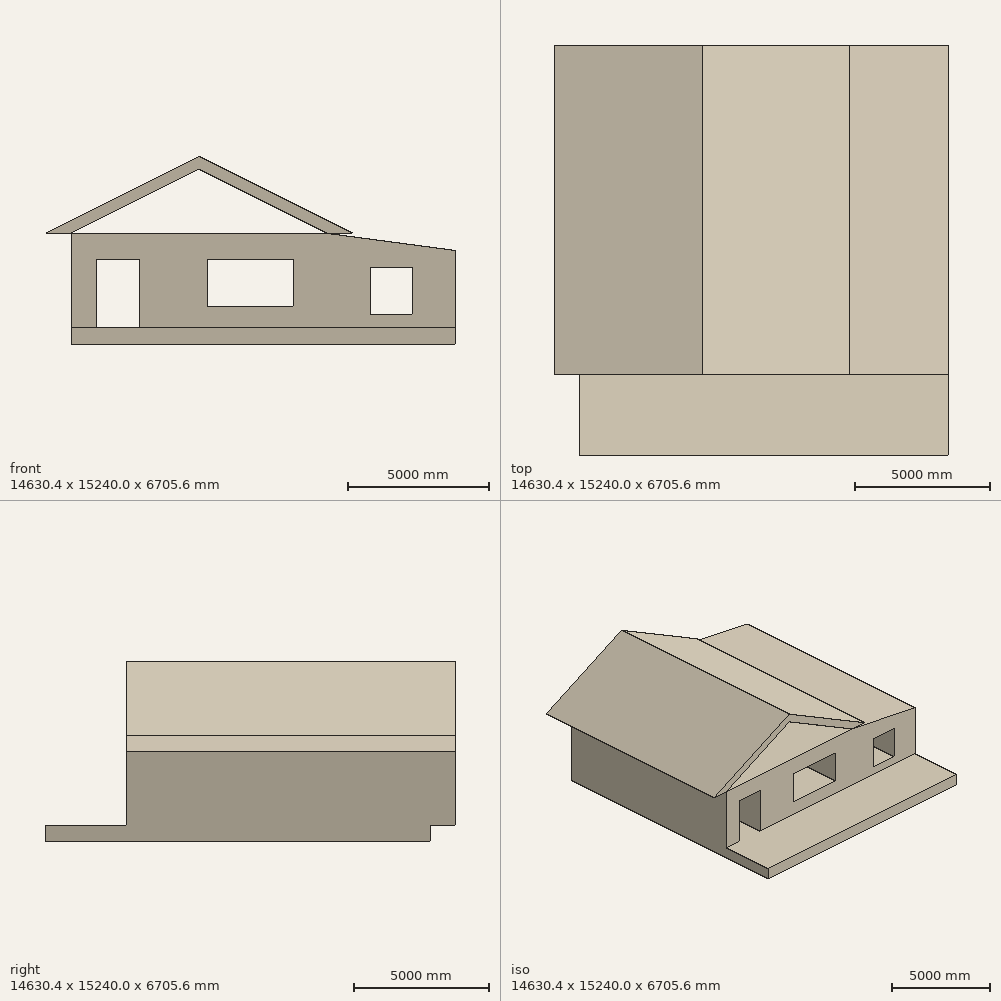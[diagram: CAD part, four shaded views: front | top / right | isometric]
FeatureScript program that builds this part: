
annotation { "Feature Type Name" : "Feature", "Feature Type Description" : "" }
export const myFeature = defineFeature(function(context is Context, id is Id, definition is map)
    precondition{}
    {
        {
            var Q0;
            Q0=qCreatedBy(makeId("Front.planeOp"),FACE);
            var sketch = newSketch(context, id + "F0", { "sketchPlane" : qUnion([Q0])});
            skLineSegment(sketch, "E0", {"start": v(0, 0) * mm, "end": v(-4572, 0) * mm});
            skLineSegment(sketch, "E1", {"start": v(0, 0) * mm, "end": v(4572, 0) * mm});
            skLineSegment(sketch, "E2", {"start": v(0, 0) * mm, "end": v(0, 2286) * mm, "construction": true});
            skLineSegment(sketch, "E3", {"start": v(-4572, 0) * mm, "end": v(-5486.4, 0) * mm});
            skLineSegment(sketch, "E4", {"start": v(4572, 0) * mm, "end": v(5486.4, 0) * mm});
            skLineSegment(sketch, "E5", {"start": v(-4572, 0) * mm, "end": v(0, 2286) * mm});
            skLineSegment(sketch, "E6", {"start": v(4572, 0) * mm, "end": v(0, 2286) * mm});
            skLineSegment(sketch, "E7", {"start": v(0, 2286) * mm, "end": v(0, 2743.2) * mm});
            skLineSegment(sketch, "E8", {"start": v(-5486.4, 0) * mm, "end": v(0, 2743.2) * mm});
            skLineSegment(sketch, "E9", {"start": v(5486.4, 0) * mm, "end": v(0, 2743.2) * mm});
            skLineSegment(sketch, "E10", {"start": v(-4572, 0) * mm, "end": v(-4572, -3352.8) * mm});
            skLineSegment(sketch, "E11", {"start": v(-4572, -3352.8) * mm, "end": v(4572, -3352.8) * mm});
            skLineSegment(sketch, "E12", {"start": v(4572, 0) * mm, "end": v(4572, -3352.8) * mm});
            skLineSegment(sketch, "E13", {"start": v(-4572, -3352.8) * mm, "end": v(-4572, -3962.4) * mm});
            skLineSegment(sketch, "E14", {"start": v(-4572, -3962.4) * mm, "end": v(4572, -3962.4) * mm});
            skLineSegment(sketch, "E15", {"start": v(4572, -3352.8) * mm, "end": v(4572, -3962.4) * mm});
            skLineSegment(sketch, "E16", {"start": v(4572, -3352.8) * mm, "end": v(9144, -3352.8) * mm});
            skLineSegment(sketch, "E17", {"start": v(4572, -3962.4) * mm, "end": v(9144, -3962.4) * mm});
            skLineSegment(sketch, "E18", {"start": v(9144, -3352.8) * mm, "end": v(9144, -3962.4) * mm});
            skLineSegment(sketch, "E19", {"start": v(9144, -3352.8) * mm, "end": v(9144, -609.6) * mm});
            skLineSegment(sketch, "E20", {"start": v(9144, -609.6) * mm, "end": v(4572, 0) * mm});
            skLineSegment(sketch, "E21", {"start": v(9144, -609.6) * mm, "end": v(9144, -1219.2) * mm});
            skLineSegment(sketch, "E22", {"start": v(9144, -1219.2) * mm, "end": v(4572.83, -609.71) * mm});
            skLineSegment(sketch, "E23", {"start": v(-3352.8, -3352.8) * mm, "end": v(-3352.8, -1219.2) * mm});
            skLineSegment(sketch, "E24", {"start": v(-3352.8, -1219.2) * mm, "end": v(-2438.4, -1219.2) * mm});
            skLineSegment(sketch, "E25", {"start": v(-2438.4, -1219.2) * mm, "end": v(-2438.4, -3352.8) * mm});
            skLineSegment(sketch, "E26.0", {"start": v(-2133.6, -914.4) * mm, "end": v(-2133.6, -3352.8) * mm});
            skLineSegment(sketch, "E26.1", {"start": v(-3657.6, -914.4) * mm, "end": v(-2133.6, -914.4) * mm});
            skLineSegment(sketch, "E26.2", {"start": v(-3657.6, -3353.8) * mm, "end": v(-3657.6, -914.4) * mm});
            skLineSegment(sketch, "E27.bottom", {"start": v(457.2, -1066.8) * mm, "end": v(3200.4, -1066.8) * mm});
            skLineSegment(sketch, "E27.top", {"start": v(457.2, -2438.4) * mm, "end": v(3200.4, -2438.4) * mm});
            skLineSegment(sketch, "E27.left", {"start": v(457.2, -1066.8) * mm, "end": v(457.2, -2438.4) * mm});
            skLineSegment(sketch, "E27.right", {"start": v(3200.4, -1066.8) * mm, "end": v(3200.4, -2438.4) * mm});
            skLineSegment(sketch, "E28.0", {"start": v(304.8, -2590.8) * mm, "end": v(3352.8, -2590.8) * mm});
            skLineSegment(sketch, "E28.1", {"start": v(304.8, -914.4) * mm, "end": v(304.8, -2590.8) * mm});
            skLineSegment(sketch, "E28.2", {"start": v(304.8, -914.4) * mm, "end": v(3352.8, -914.4) * mm});
            skLineSegment(sketch, "E28.3", {"start": v(3352.8, -914.4) * mm, "end": v(3352.8, -2590.8) * mm});
            skLineSegment(sketch, "E29.bottom", {"start": v(6248.4, -1371.6) * mm, "end": v(7467.6, -1371.6) * mm});
            skLineSegment(sketch, "E29.top", {"start": v(6248.4, -2743.2) * mm, "end": v(7467.6, -2743.2) * mm});
            skLineSegment(sketch, "E29.left", {"start": v(6248.4, -1371.6) * mm, "end": v(6248.4, -2743.2) * mm});
            skLineSegment(sketch, "E29.right", {"start": v(7467.6, -1371.6) * mm, "end": v(7467.6, -2743.2) * mm});
            skLineSegment(sketch, "E30.0", {"start": v(6096, -2895.6) * mm, "end": v(7620, -2895.6) * mm});
            skLineSegment(sketch, "E30.1", {"start": v(6096, -1219.2) * mm, "end": v(6096, -2895.6) * mm});
            skLineSegment(sketch, "E30.2", {"start": v(6096, -1219.2) * mm, "end": v(7620, -1219.2) * mm});
            skLineSegment(sketch, "E30.3", {"start": v(7620, -1219.2) * mm, "end": v(7620, -2895.6) * mm});
            skText(sketch, "E31", { "text": "Property of Whitney Gates", "fontName": "OpenSans-Regular.ttf"});
            const initialGuessF0  = {"E31": [-6.10782, 3.01593, 1, 0, 1.31451]};
            skSetInitialGuess(sketch, initialGuessF0);
            skSolve(sketch);
        }
        {
            var Q0;
            Q0=makeQuery(id+"F0.imprint","IMPRINT",FACE,{"disambiguationData":[TD([[makeQuery(id+"F0.imprint","IMPRINT",EDGE,{"derivedFrom":sQuery(id+"F0.wireOp",EDGE,"E3")}),-1.0]])]});
            var Q1;
            Q1=makeQuery(id+"F0.imprint","IMPRINT",FACE,{"disambiguationData":[TD([[makeQuery(id+"F0.imprint","IMPRINT",EDGE,{"derivedFrom":sQuery(id+"F0.wireOp",EDGE,"E4")}),1.0]])]});
            extrude(context, id + "F1", {"entities" : qUnion([Q0, Q1]), "depth" : 30.48 * mm, "offsetDistance" : 30.48 * mm, "hasSecondDirection" : true, "secondDirectionOppositeDirection" : true, "secondDirectionDepth" : 12192 * mm});
        }
        {
            var Q0;
            Q0=makeQuery(id+"F0.imprint","IMPRINT",FACE,{"disambiguationData":[TD([[makeQuery(id+"F0.imprint","IMPRINT",EDGE,{"derivedFrom":sQuery(id+"F0.wireOp",EDGE,"E15")}),1.0]])]});
            var Q1;
            {var subQ5=sQuery(id+"F0.wireOp",EDGE,"E13");Q1=makeQuery(id+"F0.imprint","IMPRINT",FACE,{"disambiguationData":[TD([[makeQuery(id+"F0.imprint","IMPRINT",EDGE,{"derivedFrom":subQ5}),1.0]])]});}
            extrude(context, id + "F2", {"entities" : qUnion([Q0, Q1]), "depth" : 3048 * mm, "offsetDistance" : 30.48 * mm, "hasSecondDirection" : true, "secondDirectionOppositeDirection" : true, "secondDirectionDepth" : 11277.6 * mm});
        }
        {
            var Q0;
            Q0=makeQuery(id+"F0.imprint","IMPRINT",FACE,{"disambiguationData":[TD([[makeQuery(id+"F0.imprint","IMPRINT",EDGE,{"derivedFrom":sQuery(id+"F0.wireOp",EDGE,"E12")}),1.0]])]});
            extrude(context, id + "F3", {"entities" : qUnion([Q0]), "operationType" : NewBodyOperationType.ADD, "oppositeDirection" : true, "depth" : 12192 * mm, "offsetDistance" : 30.48 * mm, "hasSecondDirection" : true, "secondDirectionOppositeDirection" : false, "secondDirectionDepth" : 30.48 * mm});
        }
        {
            var Q0;
            Q0=makeQuery(id+"F0.imprint","IMPRINT",FACE,{"disambiguationData":[TD([[makeQuery(id+"F0.imprint","IMPRINT",EDGE,{"derivedFrom":sQuery(id+"F0.wireOp",EDGE,"E0")}),1.0]])]});
            extrude(context, id + "F4", {"entities" : qUnion([Q0]), "operationType" : NewBodyOperationType.ADD, "oppositeDirection" : true, "depth" : 11277.6 * mm, "offsetDistance" : 30.48 * mm, "hasSecondDirection" : true, "secondDirectionOppositeDirection" : false, "secondDirectionDepth" : 30.48 * mm});
        }
    });
